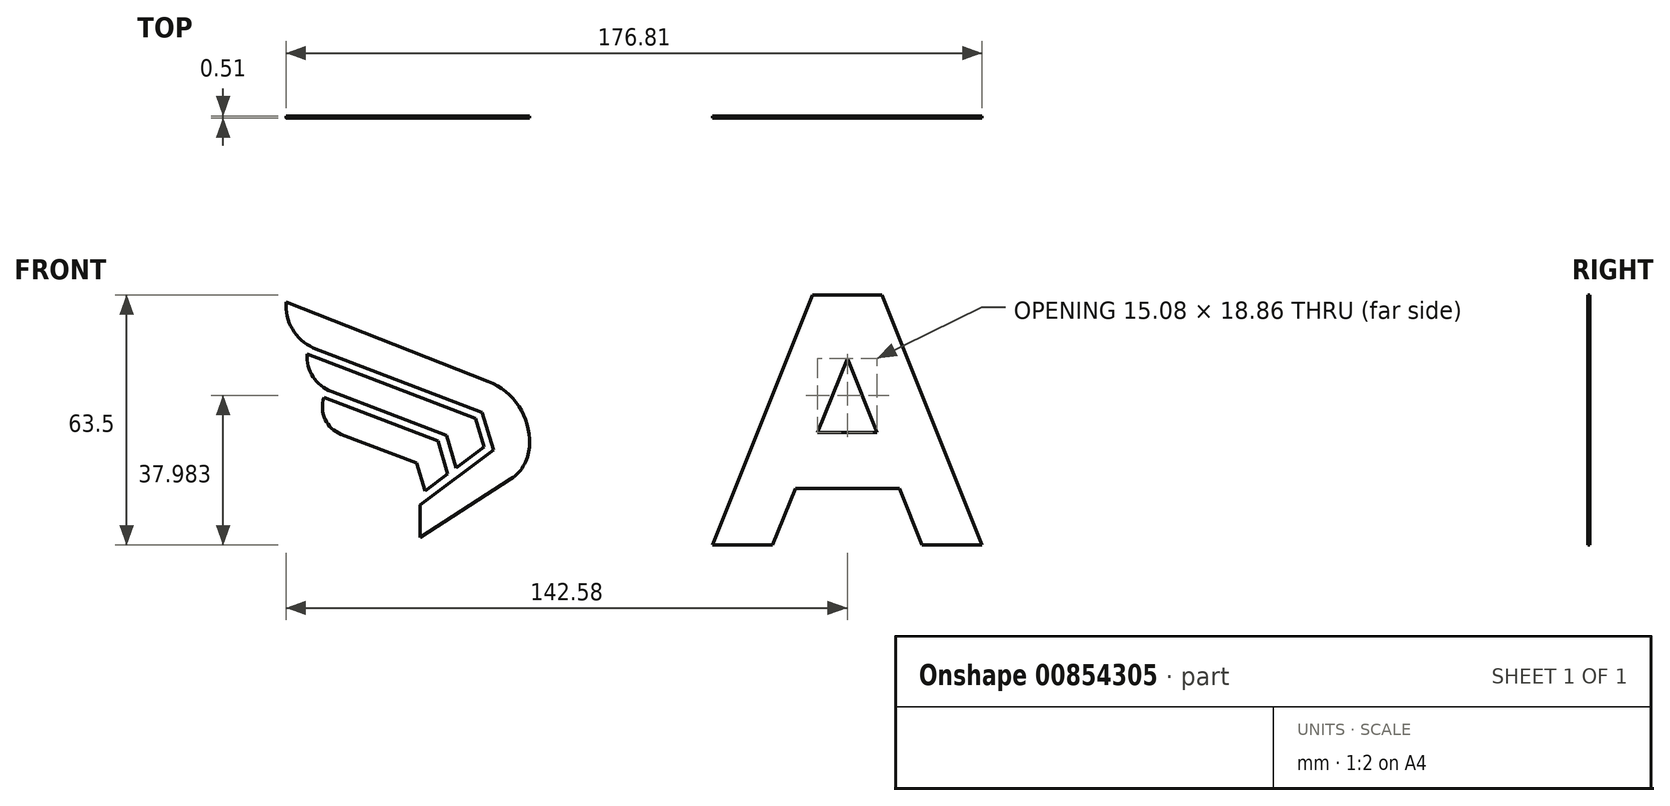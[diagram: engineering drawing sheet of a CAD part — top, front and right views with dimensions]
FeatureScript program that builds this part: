
annotation { "Feature Type Name" : "Feature", "Feature Type Description" : "" }
export const myFeature = defineFeature(function(context is Context, id is Id, definition is map)
    precondition{}
    {
        {
            var Q0;
            Q0=qCreatedBy(makeId("Front.planeOp"),FACE);
            var sketch = newSketch(context, id + "F0", { "sketchPlane" : qUnion([Q0])});
            skLineSegment(sketch, "E0", {"start": v(0, 0) * mm, "end": v(0, -63.5) * mm, "construction": true});
            skLineSegment(sketch, "E1", {"start": v(0, 0) * mm, "end": v(-8.84, 0) * mm});
            skLineSegment(sketch, "E2", {"start": v(0, 0) * mm, "end": v(-39.16, 0) * mm, "construction": true});
            skLineSegment(sketch, "E3", {"start": v(0, -63.5) * mm, "end": v(-37.9, -63.5) * mm, "construction": true});
            skLineSegment(sketch, "E4", {"start": v(-8.84, 0) * mm, "end": v(-34.23, -63.5) * mm});
            skLineSegment(sketch, "E5", {"start": v(-34.23, -63.5) * mm, "end": v(-18.95, -63.5) * mm});
            skLineSegment(sketch, "E6", {"start": v(-18.95, -63.5) * mm, "end": v(-13.21, -49.13) * mm});
            skLineSegment(sketch, "E7", {"start": v(-13.21, -49.13) * mm, "end": v(0, -49.13) * mm});
            skLineSegment(sketch, "E8", {"start": v(0, -16.09) * mm, "end": v(-7.54, -34.95) * mm});
            skLineSegment(sketch, "E9", {"start": v(-7.54, -34.95) * mm, "end": v(0, -34.95) * mm});
            skLineSegment(sketch, "E10", {"start": v(-18.95, -63.5) * mm, "end": v(0, -16.09) * mm, "construction": true});
            skLineSegment(sketch, "E11.MirrorCS", {"start": v(8.84, 0) * mm, "end": v(34.23, -63.5) * mm});
            skLineSegment(sketch, "E12.MirrorCS", {"start": v(7.54, -34.95) * mm, "end": v(0, -34.95) * mm});
            skLineSegment(sketch, "E13.MirrorCS", {"start": v(34.23, -63.5) * mm, "end": v(18.95, -63.5) * mm});
            skLineSegment(sketch, "E14.MirrorCS", {"start": v(0, 0) * mm, "end": v(8.84, 0) * mm});
            skLineSegment(sketch, "E15.MirrorCS", {"start": v(18.95, -63.5) * mm, "end": v(0, -16.09) * mm, "construction": true});
            skLineSegment(sketch, "E16.MirrorCS", {"start": v(0, -16.09) * mm, "end": v(7.54, -34.95) * mm});
            skLineSegment(sketch, "E17.MirrorCS", {"start": v(13.21, -49.13) * mm, "end": v(0, -49.13) * mm});
            skLineSegment(sketch, "E18.MirrorCS", {"start": v(18.95, -63.5) * mm, "end": v(13.21, -49.13) * mm});
            skLineSegment(sketch, "E19", {"start": v(-4.8, -28.08) * mm, "end": v(-17.96, -22.81) * mm, "construction": true});
            skLineSegment(sketch, "E20", {"start": v(3.77, -34.95) * mm, "end": v(3.77, -49.13) * mm, "construction": true});
            skSolve(sketch);
        }
        {
            var Q0;
            Q0=makeQuery(id+"F0.imprint","IMPRINT",FACE,{"disambiguationData":[TD([[makeQuery(id+"F0.imprint","IMPRINT",EDGE,{"derivedFrom":sQuery(id+"F0.wireOp",EDGE,"E1")}),1.0]])]});
            extrude(context, id + "F1", {"entities" : qUnion([Q0]), "depth" : 0.5 * mm, "offsetDistance" : 25.4 * mm});
        }
        {
            var Q0;
            Q0=qCreatedBy(makeId("Front.planeOp"),FACE);
            var sketch = newSketch(context, id + "F2", { "sketchPlane" : qUnion([Q0])});
            skLineSegment(sketch, "E21", {"start": v(-108.54, -61.55) * mm, "end": v(-85.5, -46.71) * mm});
            skLineSegment(sketch, "E22", {"start": v(-91.2, -21.94) * mm, "end": v(-142.53, -1.71) * mm});
            skArc(sketch, "E23", {"start": v(-142.53, -1.71) * mm, "mid": v(-140.98, -8.67) * mm, "end": v(-135.66, -13.42) * mm});
            skLineSegment(sketch, "E24", {"start": v(-135.66, -13.42) * mm, "end": v(-92.73, -29.85) * mm});
            skLineSegment(sketch, "E25", {"start": v(-92.73, -29.85) * mm, "end": v(-89.84, -39.37) * mm});
            skLineSegment(sketch, "E26", {"start": v(-89.84, -39.37) * mm, "end": v(-108.54, -53.3) * mm});
            skLineSegment(sketch, "E27", {"start": v(-108.54, -53.3) * mm, "end": v(-108.54, -61.55) * mm});
            skLineSegment(sketch, "E28", {"start": v(-99.35, -43.88) * mm, "end": v(-92.24, -38.58) * mm});
            skLineSegment(sketch, "E29", {"start": v(-92.24, -38.58) * mm, "end": v(-94.42, -31.42) * mm});
            skLineSegment(sketch, "E30", {"start": v(-94.42, -31.42) * mm, "end": v(-137.3, -15) * mm});
            skLineSegment(sketch, "E31", {"start": v(-132.97, -26) * mm, "end": v(-104.02, -37.09) * mm});
            skLineSegment(sketch, "E32", {"start": v(-104.02, -37.09) * mm, "end": v(-101.48, -45.46) * mm});
            skLineSegment(sketch, "E33", {"start": v(-99.35, -43.88) * mm, "end": v(-101.83, -35.7) * mm});
            skLineSegment(sketch, "E34", {"start": v(-101.83, -35.7) * mm, "end": v(-131.04, -24.53) * mm});
            skLineSegment(sketch, "E35", {"start": v(-101.48, -45.46) * mm, "end": v(-107.28, -49.78) * mm});
            skLineSegment(sketch, "E36", {"start": v(-107.28, -49.78) * mm, "end": v(-109.43, -42.7) * mm});
            skLineSegment(sketch, "E37", {"start": v(-109.43, -42.7) * mm, "end": v(-128.55, -35.37) * mm});
            skArc(sketch, "E38", {"start": v(-137.3, -15) * mm, "mid": v(-135.7, -20.78) * mm, "end": v(-131.04, -24.53) * mm});
            skArc(sketch, "E39", {"start": v(-132.97, -26) * mm, "mid": v(-132.64, -31.58) * mm, "end": v(-128.55, -35.37) * mm});
            skArc(sketch, "E40", {"start": v(-85.5, -46.71) * mm, "mid": v(-82, -42.93) * mm, "end": v(-80.76, -37.93) * mm});
            skArc(sketch, "E41", {"start": v(-80.76, -37.93) * mm, "mid": v(-83.44, -28.27) * mm, "end": v(-91.2, -21.94) * mm});
            skLineSegment(sketch, "E42", {"start": v(-107.87, -26.27) * mm, "end": v(-107.13, -24.34) * mm, "construction": true});
            skLineSegment(sketch, "E43", {"start": v(-112.5, -33.84) * mm, "end": v(-111.76, -31.91) * mm});
            skLineSegment(sketch, "E44", {"start": v(-93.33, -35) * mm, "end": v(-91.35, -34.4) * mm});
            skLineSegment(sketch, "E45", {"start": v(-95.1, -43.29) * mm, "end": v(-96.33, -41.63) * mm});
            skSolve(sketch);
        }
        {
            var Q0;
            Q0=makeQuery(id+"F2.imprint","IMPRINT",FACE,{"disambiguationData":[TD([[makeQuery(id+"F2.imprint","IMPRINT",EDGE,{"derivedFrom":sQuery(id+"F2.wireOp",EDGE,"E21")}),1.0]])]});
            var Q1;
            {var subQ0=sQuery(id+"F2.wireOp",EDGE,"E30");Q1=makeQuery(id+"F2.imprint","IMPRINT",FACE,{"disambiguationData":[TD([[makeQuery(id+"F2.imprint","IMPRINT",EDGE,{"derivedFrom":subQ0}),1.0]])]});}
            var Q2;
            {var subQ0=sQuery(id+"F2.wireOp",EDGE,"E32");Q2=makeQuery(id+"F2.imprint","IMPRINT",FACE,{"disambiguationData":[TD([[makeQuery(id+"F2.imprint","IMPRINT",EDGE,{"derivedFrom":subQ0}),-1.0]])]});}
            extrude(context, id + "F3", {"entities" : qUnion([Q0, Q1, Q2]), "depth" : 0.5 * mm, "offsetDistance" : 25.4 * mm});
        }
    });
